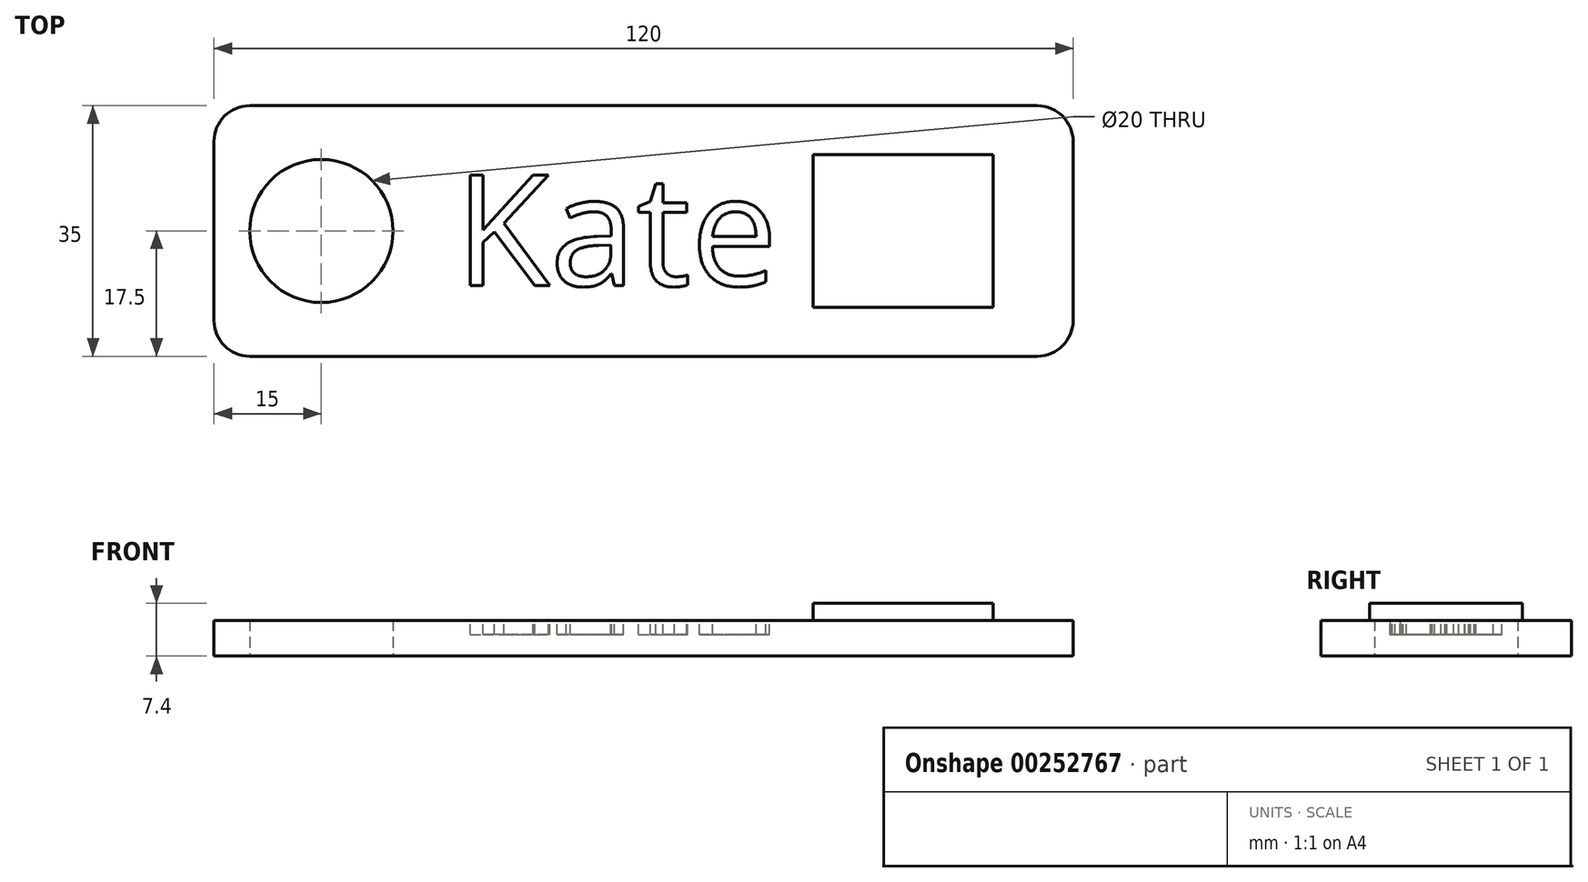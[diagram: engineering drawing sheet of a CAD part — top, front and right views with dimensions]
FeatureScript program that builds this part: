
annotation { "Feature Type Name" : "Feature", "Feature Type Description" : "" }
export const myFeature = defineFeature(function(context is Context, id is Id, definition is map)
    precondition{}
    {
        {
            var Q0;
            Q0=qCreatedBy(makeId("Top.planeOp"),FACE);
            var sketch = newSketch(context, id + "F0", { "sketchPlane" : qUnion([Q0])});
            skLineSegment(sketch, "E0.bottom", {"start": v(-60, -17.5) * mm, "end": v(60, -17.5) * mm});
            skLineSegment(sketch, "E0.top", {"start": v(-60, 17.5) * mm, "end": v(60, 17.5) * mm});
            skLineSegment(sketch, "E0.left", {"start": v(-60, -17.5) * mm, "end": v(-60, 17.5) * mm});
            skLineSegment(sketch, "E0.right", {"start": v(60, -17.5) * mm, "end": v(60, 17.5) * mm});
            skPoint(sketch, "E0.middle", {"position": v(0, 0) * mm});
            skCircle(sketch, "E1", {"center": v(-45, 0) * mm, "radius": 10 * mm});
            skSolve(sketch);
        }
        {
            var Q0;
            Q0=makeQuery(id+"F0.imprint","IMPRINT",FACE,{"disambiguationData":[TD([[makeQuery(id+"F0.imprint","IMPRINT",EDGE,{"derivedFrom":sQuery(id+"F0.wireOp",EDGE,"E0.bottom")}),1.0]])]});
            extrude(context, id + "F1", {"entities" : qUnion([Q0]), "depth" : 5 * mm});
        }
        {
            var Q0;
            Q0=makeQuery(id+"F1.opExtrude","SWEPT_EDGE",EDGE,{"disambiguationData":[OSD([sQuery(id+"F0.wireOp",EDGE,"E0.bottom"),sQuery(id+"F0.wireOp",EDGE,"E0.right")])]});
            fillet(context, id + "F2", {"entities" : qUnion([Q0]), "radius" : 5 * mm, "tangentPropagation" : true, "allowEdgeOverflow" : false});
        }
        {
            var Q0;
            Q0=makeQuery(id+"F1.opExtrude","SWEPT_EDGE",EDGE,{"disambiguationData":[OSD([sQuery(id+"F0.wireOp",EDGE,"E0.top"),sQuery(id+"F0.wireOp",EDGE,"E0.right")])]});
            fillet(context, id + "F3", {"entities" : qUnion([Q0]), "radius" : 5 * mm, "tangentPropagation" : true, "allowEdgeOverflow" : false});
        }
        {
            var Q0;
            Q0=makeQuery(id+"F1.opExtrude","SWEPT_EDGE",EDGE,{"disambiguationData":[OSD([sQuery(id+"F0.wireOp",EDGE,"E0.bottom"),sQuery(id+"F0.wireOp",EDGE,"E0.left")])]});
            fillet(context, id + "F4", {"entities" : qUnion([Q0]), "radius" : 5 * mm, "tangentPropagation" : true, "allowEdgeOverflow" : false});
        }
        {
            var Q0;
            Q0=makeQuery(id+"F1.opExtrude","CAP_FACE",FACE,{"disambiguationData":[OSD([sQuery(id+"F0.wireOp",EDGE,"E0.bottom"),sQuery(id+"F0.wireOp",EDGE,"E0.top"),sQuery(id+"F0.wireOp",EDGE,"E0.left"),sQuery(id+"F0.wireOp",EDGE,"E0.right"),sQuery(id+"F0.wireOp",EDGE,"E1")])],"isStart":false});
            var sketch = newSketch(context, id + "F5", { "sketchPlane" : qUnion([Q0])});
            skText(sketch, "E2", { "text": "Kate", "fontName": "OpenSans-Regular.ttf"});
            const initialGuessF5  = {"E2": [-0.02634, -0.00763, 1, 0, 0.01557]};
            skSetInitialGuess(sketch, initialGuessF5);
            skSolve(sketch);
        }
        {
            var Q0;
            Q0=makeQuery(id+"F5.imprint","IMPRINT",FACE,{"disambiguationData":[TD([[makeQuery(id+"F5.imprint","IMPRINT",EDGE,{"derivedFrom":sQuery(id+"F5.wireOp",EDGE,"E2.sketch_text.stroke-0")}),1.0]])]});
            var sketch = newSketch(context, id + "F6", { "sketchPlane" : qUnion([Q0])});
            skSolve(sketch);
        }
        {
            var Q0;
            Q0=makeQuery(id+"F1.opExtrude","SWEPT_EDGE",EDGE,{"disambiguationData":[OSD([sQuery(id+"F0.wireOp",EDGE,"E0.top"),sQuery(id+"F0.wireOp",EDGE,"E0.left")])]});
            fillet(context, id + "F7", {"entities" : qUnion([Q0]), "radius" : 5 * mm, "tangentPropagation" : true, "allowEdgeOverflow" : false});
        }
        {
            var Q0;
            Q0 = qSketchRegion(id + "F5", true);
            extrude(context, id + "F8", {"entities" : qUnion([Q0]), "operationType" : NewBodyOperationType.REMOVE, "oppositeDirection" : true, "depth" : 2 * mm});
        }
        {
            var Q0;
            Q0=makeQuery(id+"F6.imprint","IMPRINT",FACE,{"disambiguationData":[TD([[makeQuery(id+"F6.imprint","IMPRINT",EDGE,{"derivedFrom":makeQuery(id+"F5.imprint","IMPRINT",EDGE,{"derivedFrom":sQuery(id+"F5.wireOp",EDGE,"E2.sketch_text.stroke-0")})}),1.0]])]});
            var sketch = newSketch(context, id + "F9", { "sketchPlane" : qUnion([Q0])});
            skLineSegment(sketch, "E3.bottom", {"start": v(23.68, 10.66) * mm, "end": v(48.85, 10.66) * mm});
            skLineSegment(sketch, "E3.top", {"start": v(23.68, -10.66) * mm, "end": v(48.85, -10.66) * mm});
            skLineSegment(sketch, "E3.left", {"start": v(23.68, 10.66) * mm, "end": v(23.68, -10.66) * mm});
            skLineSegment(sketch, "E3.right", {"start": v(48.85, 10.66) * mm, "end": v(48.85, -10.66) * mm});
            skSolve(sketch);
        }
        {
            var Q0;
            Q0 = qSketchRegion(id + "F9", true);
            extrude(context, id + "F10", {"entities" : qUnion([Q0]), "operationType" : NewBodyOperationType.ADD, "depth" : 2.4 * mm});
        }
    });
